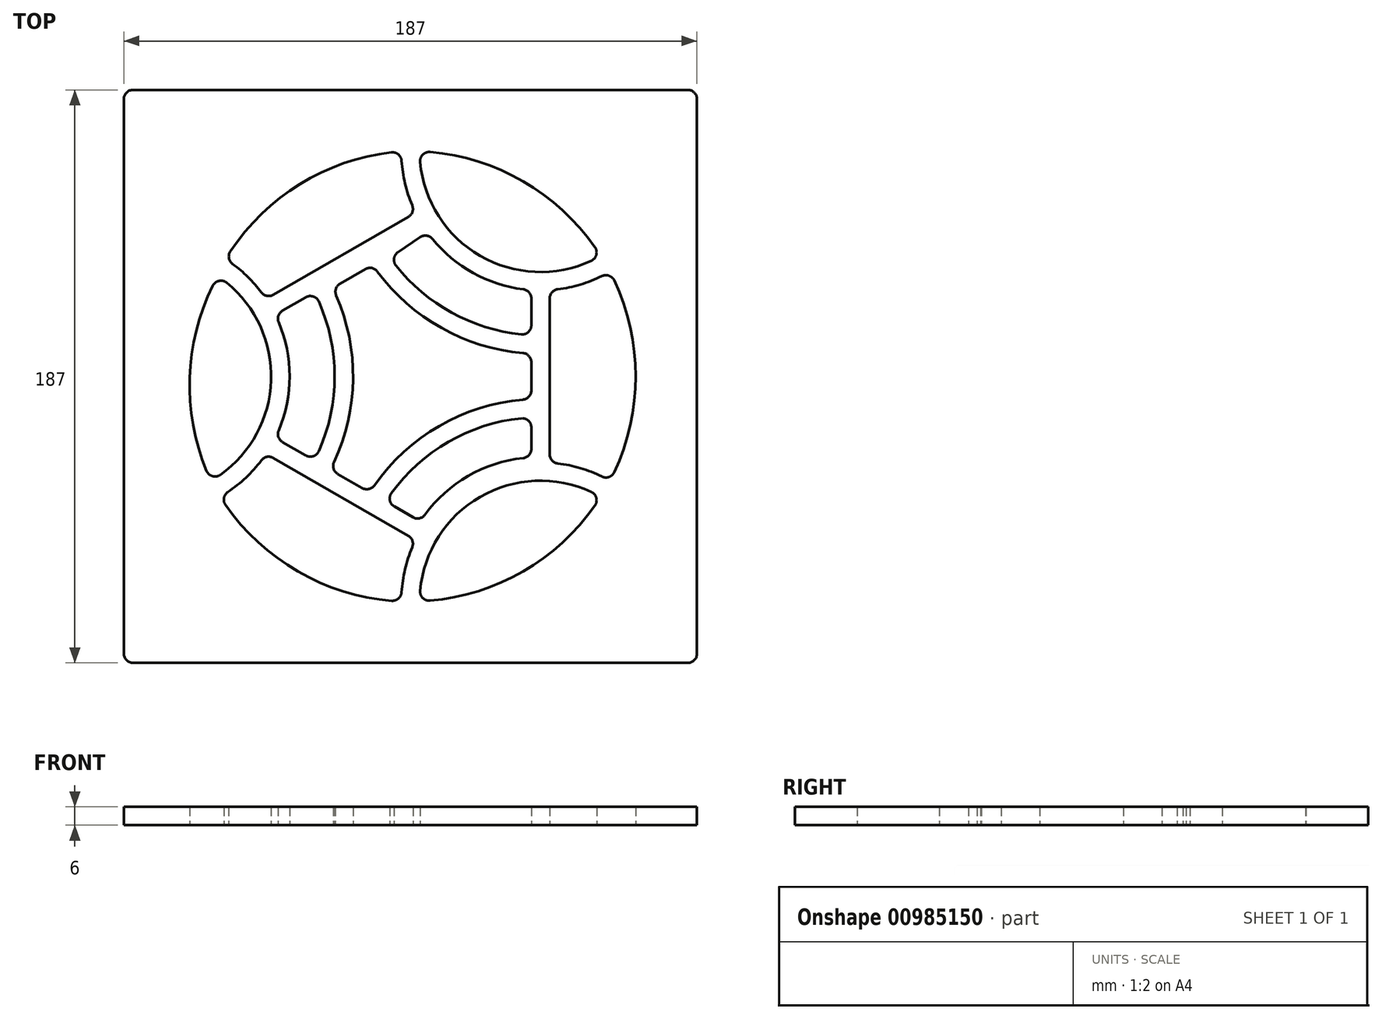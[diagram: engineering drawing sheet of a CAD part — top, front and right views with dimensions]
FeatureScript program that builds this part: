
annotation { "Feature Type Name" : "Feature", "Feature Type Description" : "" }
export const myFeature = defineFeature(function(context is Context, id is Id, definition is map)
    precondition{}
    {
        {
            var Q0;
            Q0=qCreatedBy(makeId("Top.planeOp"),FACE);
            var sketch = newSketch(context, id + "F0", { "sketchPlane" : qUnion([Q0])});
            skLineSegment(sketch, "E0.bottom", {"start": v(-81.46, 94.73) * mm, "end": v(99.54, 94.73) * mm});
            skLineSegment(sketch, "E0.top", {"start": v(-81.46, -92.27) * mm, "end": v(99.54, -92.27) * mm});
            skLineSegment(sketch, "E0.left", {"start": v(-84.46, 91.73) * mm, "end": v(-84.46, -89.27) * mm});
            skLineSegment(sketch, "E0.right", {"start": v(102.54, 91.73) * mm, "end": v(102.54, -89.27) * mm});
            skPoint(sketch, "E1.center", {"position": v(9.04, 1.23) * mm});
            skArc(sketch, "E2.0.left", {"start": v(-49, 37.9) * mm, "mid": v(-43.97, 33.62) * mm, "end": v(-39.6, 28.64) * mm});
            skArc(sketch, "E2.0.right", {"start": v(-50.9, 31.78) * mm, "mid": v(-36.42, -0.1) * mm, "end": v(-53, -30.92) * mm});
            skLineSegment(sketch, "E2.1.left", {"start": v(-35.7, 27.86) * mm, "end": v(8.35, 53.3) * mm});
            skLineSegment(sketch, "E2.1.right", {"start": v(-32.7, 22.66) * mm, "end": v(-25.12, 27.04) * mm});
            skArc(sketch, "E2.2.left", {"start": v(45.74, 8.83) * mm, "mid": v(19.14, 17.02) * mm, "end": v(-1.73, 35.42) * mm});
            skArc(sketch, "E2.2.right", {"start": v(45.16, 14.92) * mm, "mid": v(22.46, 22.04) * mm, "end": v(4.3, 37.42) * mm});
            skArc(sketch, "E2.3.left", {"start": v(-15.2, 27.65) * mm, "mid": v(-9.7, 0.37) * mm, "end": v(-15.9, -26.75) * mm});
            skArc(sketch, "E2.3.right", {"start": v(-20.87, 25.67) * mm, "mid": v(-15.69, 1.23) * mm, "end": v(-20.87, -23.2) * mm});
            skArc(sketch, "E2.4.left", {"start": v(-2.72, -34.35) * mm, "mid": v(18.4, -14.99) * mm, "end": v(45.74, -6.38) * mm});
            skArc(sketch, "E2.4.right", {"start": v(2.83, -36.9) * mm, "mid": v(21.4, -20.18) * mm, "end": v(45.16, -12.46) * mm});
            skLineSegment(sketch, "E2.5.left", {"start": v(54.47, 26.67) * mm, "end": v(54.47, -24.2) * mm});
            skLineSegment(sketch, "E2.5.right", {"start": v(48.47, 26.67) * mm, "end": v(48.47, 17.9) * mm});
            skArc(sketch, "E2.6.left", {"start": v(71.5, 33.95) * mm, "mid": v(64.48, 31.2) * mm, "end": v(57.1, 29.64) * mm});
            skArc(sketch, "E2.6.right", {"start": v(68.05, 38.94) * mm, "mid": v(31.76, 40.58) * mm, "end": v(12.2, 71.2) * mm});
            skArc(sketch, "E2.7.left", {"start": v(6.14, -69.23) * mm, "mid": v(7.27, -61.77) * mm, "end": v(9.62, -54.6) * mm});
            skArc(sketch, "E2.7.right", {"start": v(12.2, -68.73) * mm, "mid": v(31.76, -38.12) * mm, "end": v(68.05, -36.49) * mm});
            skLineSegment(sketch, "E2.8.left", {"start": v(8.35, -50.84) * mm, "end": v(-35.7, -25.4) * mm});
            skLineSegment(sketch, "E2.8.right", {"start": v(9.85, -44.78) * mm, "end": v(3.76, -41.26) * mm});
            skArc(sketch, "E3", {"start": v(-55.48, 30.78) * mm, "mid": v(-62.98, 0.8) * mm, "end": v(-57.5, -29.61) * mm});
            skArc(sketch, "E4", {"start": v(-51.32, -40.71) * mm, "mid": v(-27.71, -62.42) * mm, "end": v(2.9, -72.02) * mm});
            skArc(sketch, "E5", {"start": v(15.45, -72) * mm, "mid": v(45.79, -62.42) * mm, "end": v(69.25, -40.93) * mm});
            skArc(sketch, "E6", {"start": v(75.54, -30.07) * mm, "mid": v(82.54, 1.23) * mm, "end": v(75.54, 32.53) * mm});
            skArc(sketch, "E7", {"start": v(69.25, 43.39) * mm, "mid": v(45.79, 64.88) * mm, "end": v(15.45, 74.45) * mm});
            skArc(sketch, "E8", {"start": v(2.8, 74.35) * mm, "mid": v(-27.03, 63.94) * mm, "end": v(-49.73, 41.98) * mm});
            skArc(sketch, "E9", {"start": v(-39.6, -26.19) * mm, "mid": v(-44.63, -31.8) * mm, "end": v(-50.53, -36.5) * mm});
            skLineSegment(sketch, "E10", {"start": v(-25.12, -24.59) * mm, "end": v(-32.7, -20.2) * mm});
            skLineSegment(sketch, "E11", {"start": v(-6.68, -35.23) * mm, "end": v(-14.68, -30.62) * mm});
            skArc(sketch, "E12", {"start": v(13.78, -43.94) * mm, "mid": v(27.82, -31.3) * mm, "end": v(45.79, -25.46) * mm});
            skArc(sketch, "E13", {"start": v(57.1, -27.19) * mm, "mid": v(64.48, -28.74) * mm, "end": v(71.5, -31.49) * mm});
            skLineSegment(sketch, "E14", {"start": v(48.47, -15.44) * mm, "end": v(48.47, -22.48) * mm});
            skLineSegment(sketch, "E15", {"start": v(48.47, 5.84) * mm, "end": v(48.47, -3.39) * mm});
            skArc(sketch, "E16", {"start": v(45.85, 29.64) * mm, "mid": v(29.45, 34.99) * mm, "end": v(16.23, 46.06) * mm});
            skArc(sketch, "E17", {"start": v(-33.97, 18.9) * mm, "mid": v(-30.4, 1.23) * mm, "end": v(-33.97, -16.44) * mm});
            skLineSegment(sketch, "E18", {"start": v(-13.94, 31.45) * mm, "end": v(-5.64, 36.24) * mm});
            skLineSegment(sketch, "E19", {"start": v(4.98, 41.77) * mm, "end": v(12.22, 46.65) * mm});
            skArc(sketch, "E20", {"start": v(9.62, 57.06) * mm, "mid": v(7.28, 64.18) * mm, "end": v(6.15, 71.58) * mm});
            skArc(sketch, "E21.filletArc", {"start": v(-49.73, 41.98) * mm, "mid": v(-50.19, 39.8) * mm, "end": v(-49, 37.9) * mm});
            skArc(sketch, "E22.filletArc", {"start": v(-50.9, 31.78) * mm, "mid": v(-53.43, 32.38) * mm, "end": v(-55.48, 30.78) * mm});
            skPoint(sketch, "E23.visualSharp", {"position": v(-38.07, 26.5) * mm});
            skArc(sketch, "E23.filletArc", {"start": v(-39.6, 28.64) * mm, "mid": v(-37.8, 27.51) * mm, "end": v(-35.7, 27.86) * mm});
            skPoint(sketch, "E24.visualSharp", {"position": v(-35.07, 21.3) * mm});
            skArc(sketch, "E24.filletArc", {"start": v(-32.7, 22.66) * mm, "mid": v(-34.05, 21.02) * mm, "end": v(-33.97, 18.9) * mm});
            skPoint(sketch, "E25.visualSharp", {"position": v(-22.3, 28.66) * mm});
            skArc(sketch, "E25.filletArc", {"start": v(-20.87, 25.67) * mm, "mid": v(-22.69, 27.3) * mm, "end": v(-25.12, 27.04) * mm});
            skPoint(sketch, "E26.visualSharp", {"position": v(-16.3, 30.08) * mm});
            skArc(sketch, "E26.filletArc", {"start": v(-13.94, 31.45) * mm, "mid": v(-15.3, 29.79) * mm, "end": v(-15.2, 27.65) * mm});
            skPoint(sketch, "E27.visualSharp", {"position": v(-3.27, 37.6) * mm});
            skArc(sketch, "E27.filletArc", {"start": v(-1.73, 35.42) * mm, "mid": v(-3.53, 36.58) * mm, "end": v(-5.64, 36.24) * mm});
            skPoint(sketch, "E28.visualSharp", {"position": v(2.37, 40) * mm});
            skArc(sketch, "E28.filletArc", {"start": v(4.98, 41.77) * mm, "mid": v(3.69, 39.74) * mm, "end": v(4.3, 37.42) * mm});
            skPoint(sketch, "E29.visualSharp", {"position": v(14.57, 48.23) * mm});
            skArc(sketch, "E29.filletArc", {"start": v(16.23, 46.06) * mm, "mid": v(14.34, 47.13) * mm, "end": v(12.22, 46.65) * mm});
            skPoint(sketch, "E30.visualSharp", {"position": v(10.71, 54.66) * mm});
            skArc(sketch, "E30.filletArc", {"start": v(8.35, 53.3) * mm, "mid": v(9.7, 54.94) * mm, "end": v(9.62, 57.06) * mm});
            skPoint(sketch, "E31.visualSharp", {"position": v(-35.07, -18.84) * mm});
            skArc(sketch, "E31.filletArc", {"start": v(-33.97, -16.44) * mm, "mid": v(-34.05, -18.56) * mm, "end": v(-32.7, -20.2) * mm});
            skPoint(sketch, "E32.visualSharp", {"position": v(-22.3, -26.2) * mm});
            skArc(sketch, "E32.filletArc", {"start": v(-25.12, -24.59) * mm, "mid": v(-22.69, -24.84) * mm, "end": v(-20.87, -23.2) * mm});
            skPoint(sketch, "E33.visualSharp", {"position": v(-17.1, -29.21) * mm});
            skArc(sketch, "E33.filletArc", {"start": v(-15.9, -26.75) * mm, "mid": v(-16.04, -28.92) * mm, "end": v(-14.68, -30.62) * mm});
            skPoint(sketch, "E34.visualSharp", {"position": v(-4.25, -36.64) * mm});
            skArc(sketch, "E34.filletArc", {"start": v(-6.68, -35.23) * mm, "mid": v(-4.53, -35.56) * mm, "end": v(-2.72, -34.35) * mm});
            skPoint(sketch, "E35.visualSharp", {"position": v(48.47, -12.2) * mm});
            skArc(sketch, "E35.filletArc", {"start": v(48.47, -15.44) * mm, "mid": v(47.48, -13.21) * mm, "end": v(45.16, -12.46) * mm});
            skPoint(sketch, "E36.visualSharp", {"position": v(48.47, -6.2) * mm});
            skArc(sketch, "E36.filletArc", {"start": v(45.74, -6.38) * mm, "mid": v(47.69, -5.42) * mm, "end": v(48.47, -3.39) * mm});
            skPoint(sketch, "E37.visualSharp", {"position": v(48.47, 8.65) * mm});
            skArc(sketch, "E37.filletArc", {"start": v(48.47, 5.84) * mm, "mid": v(47.69, 7.87) * mm, "end": v(45.74, 8.83) * mm});
            skPoint(sketch, "E38.visualSharp", {"position": v(48.47, 14.66) * mm});
            skArc(sketch, "E38.filletArc", {"start": v(45.16, 14.92) * mm, "mid": v(47.48, 15.67) * mm, "end": v(48.47, 17.9) * mm});
            skPoint(sketch, "E39.visualSharp", {"position": v(48.47, 29.4) * mm});
            skArc(sketch, "E39.filletArc", {"start": v(48.47, 26.67) * mm, "mid": v(47.72, 28.65) * mm, "end": v(45.85, 29.64) * mm});
            skPoint(sketch, "E40.visualSharp", {"position": v(-38.07, -24.04) * mm});
            skArc(sketch, "E40.filletArc", {"start": v(-35.7, -25.4) * mm, "mid": v(-37.8, -25.06) * mm, "end": v(-39.6, -26.19) * mm});
            skPoint(sketch, "E41.visualSharp", {"position": v(10.71, -52.2) * mm});
            skArc(sketch, "E41.filletArc", {"start": v(9.62, -54.6) * mm, "mid": v(9.7, -52.48) * mm, "end": v(8.35, -50.84) * mm});
            skPoint(sketch, "E42.visualSharp", {"position": v(0.95, -39.64) * mm});
            skArc(sketch, "E42.filletArc", {"start": v(2.83, -36.9) * mm, "mid": v(2.32, -39.28) * mm, "end": v(3.76, -41.26) * mm});
            skPoint(sketch, "E43.visualSharp", {"position": v(12.26, -46.17) * mm});
            skArc(sketch, "E43.filletArc", {"start": v(9.85, -44.78) * mm, "mid": v(11.97, -45.11) * mm, "end": v(13.78, -43.94) * mm});
            skPoint(sketch, "E44.visualSharp", {"position": v(48.47, -25.26) * mm});
            skArc(sketch, "E44.filletArc", {"start": v(45.79, -25.46) * mm, "mid": v(47.7, -24.48) * mm, "end": v(48.47, -22.48) * mm});
            skPoint(sketch, "E45.visualSharp", {"position": v(54.47, -26.94) * mm});
            skArc(sketch, "E45.filletArc", {"start": v(54.47, -24.2) * mm, "mid": v(55.23, -26.2) * mm, "end": v(57.1, -27.19) * mm});
            skPoint(sketch, "E46.visualSharp", {"position": v(54.47, 29.4) * mm});
            skArc(sketch, "E46.filletArc", {"start": v(57.1, 29.64) * mm, "mid": v(55.23, 28.65) * mm, "end": v(54.47, 26.67) * mm});
            skPoint(sketch, "E47.orphan", {"position": v(71.2, 40.58) * mm});
            skPoint(sketch, "E48.orphan", {"position": v(6.04, 74.73) * mm});
            skPoint(sketch, "E49.orphan", {"position": v(-56.11, -32.92) * mm});
            skPoint(sketch, "E50.newPointB", {"position": v(74.2, 35.38) * mm});
            skArc(sketch, "E50.filletArc", {"start": v(75.54, 32.53) * mm, "mid": v(73.82, 34.08) * mm, "end": v(71.5, 33.95) * mm});
            skPoint(sketch, "E51.visualSharp", {"position": v(71.14, 40.55) * mm});
            skArc(sketch, "E51.filletArc", {"start": v(68.05, 38.94) * mm, "mid": v(69.69, 40.89) * mm, "end": v(69.25, 43.39) * mm});
            skPoint(sketch, "E52.newPointA", {"position": v(12.04, 74.73) * mm});
            skArc(sketch, "E52.filletArc", {"start": v(15.45, 74.45) * mm, "mid": v(13.06, 73.58) * mm, "end": v(12.2, 71.2) * mm});
            skPoint(sketch, "E53.visualSharp", {"position": v(6.04, 74.67) * mm});
            skArc(sketch, "E53.filletArc", {"start": v(6.15, 71.58) * mm, "mid": v(5.07, 73.68) * mm, "end": v(2.8, 74.35) * mm});
            skPoint(sketch, "E54.visualSharp", {"position": v(-56.06, -32.9) * mm});
            skArc(sketch, "E54.filletArc", {"start": v(-57.5, -29.61) * mm, "mid": v(-55.56, -31.36) * mm, "end": v(-53, -30.92) * mm});
            skPoint(sketch, "E55.newPointB", {"position": v(-53.11, -38.12) * mm});
            skArc(sketch, "E55.filletArc", {"start": v(-50.53, -36.5) * mm, "mid": v(-51.8, -38.44) * mm, "end": v(-51.32, -40.71) * mm});
            skPoint(sketch, "E56.newPointA", {"position": v(6.04, -72.27) * mm});
            skArc(sketch, "E56.filletArc", {"start": v(2.9, -72.02) * mm, "mid": v(5.1, -71.3) * mm, "end": v(6.14, -69.23) * mm});
            skPoint(sketch, "E57.newPointA", {"position": v(12.04, -72.27) * mm});
            skArc(sketch, "E57.filletArc", {"start": v(12.2, -68.73) * mm, "mid": v(13.06, -71.12) * mm, "end": v(15.45, -72) * mm});
            skPoint(sketch, "E58.newPointA", {"position": v(71.2, -38.12) * mm});
            skArc(sketch, "E58.filletArc", {"start": v(69.25, -40.93) * mm, "mid": v(69.69, -38.43) * mm, "end": v(68.05, -36.49) * mm});
            skPoint(sketch, "E59.newPointA", {"position": v(74.2, -32.92) * mm});
            skArc(sketch, "E59.filletArc", {"start": v(71.5, -31.49) * mm, "mid": v(73.82, -31.63) * mm, "end": v(75.54, -30.07) * mm});
            skPoint(sketch, "E60.visualSharp", {"position": v(-84.46, 94.73) * mm});
            skArc(sketch, "E60.filletArc", {"start": v(-81.46, 94.73) * mm, "mid": v(-83.58, 93.85) * mm, "end": v(-84.46, 91.73) * mm});
            skPoint(sketch, "E61.visualSharp", {"position": v(102.54, 94.73) * mm});
            skArc(sketch, "E61.filletArc", {"start": v(102.54, 91.73) * mm, "mid": v(101.66, 93.85) * mm, "end": v(99.54, 94.73) * mm});
            skPoint(sketch, "E62.visualSharp", {"position": v(102.54, -92.27) * mm});
            skArc(sketch, "E62.filletArc", {"start": v(99.54, -92.27) * mm, "mid": v(101.66, -91.4) * mm, "end": v(102.54, -89.27) * mm});
            skPoint(sketch, "E63.visualSharp", {"position": v(-84.46, -92.27) * mm});
            skArc(sketch, "E63.filletArc", {"start": v(-84.46, -89.27) * mm, "mid": v(-83.58, -91.4) * mm, "end": v(-81.46, -92.27) * mm});
            skSolve(sketch);
        }
        {
            var Q0;
            Q0=makeQuery(id+"F0.imprint","IMPRINT",FACE,{"disambiguationData":[TD([[makeQuery(id+"F0.imprint","IMPRINT",EDGE,{"derivedFrom":sQuery(id+"F0.wireOp",EDGE,"E0.bottom")}),-1.0]])]});
            extrude(context, id + "F1", {"entities" : qUnion([Q0]), "depth" : 6 * mm, "offsetDistance" : 25 * mm});
        }
    });
